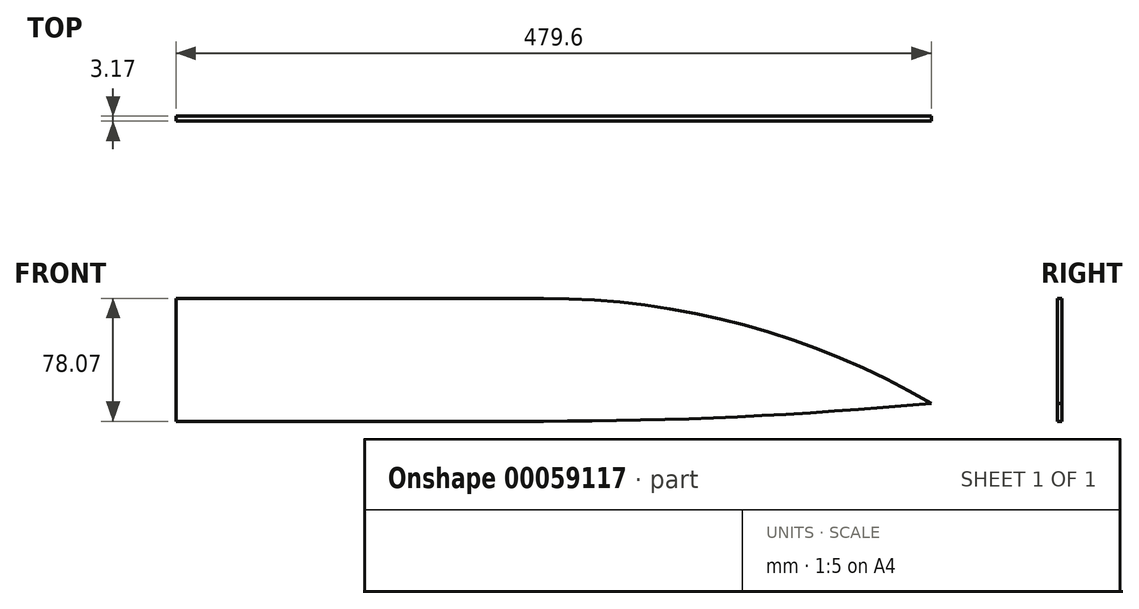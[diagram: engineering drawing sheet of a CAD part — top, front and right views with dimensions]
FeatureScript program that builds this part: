
annotation { "Feature Type Name" : "Feature", "Feature Type Description" : "" }
export const myFeature = defineFeature(function(context is Context, id is Id, definition is map)
    precondition{}
    {
        {
            var Q0;
            Q0=qCreatedBy(makeId("Front.planeOp"),FACE);
            var sketch = newSketch(context, id + "F0", { "sketchPlane" : qUnion([Q0])});
            skLineSegment(sketch, "E0", {"start": v(-232.64, 31.37) * mm, "end": v(0.7, 31.37) * mm});
            skLineSegment(sketch, "E1", {"start": v(-232.64, -46.7) * mm, "end": v(-232.64, 31.37) * mm});
            skLineSegment(sketch, "E2", {"start": v(0.7, -46.7) * mm, "end": v(-232.64, -46.7) * mm});
            skArc(sketch, "E3", {"start": v(246.96, -35.25) * mm, "mid": v(128.26, 14.42) * mm, "end": v(0.7, 31.37) * mm});
            skArc(sketch, "E4", {"start": v(0.7, -46.7) * mm, "mid": v(123.96, -43.83) * mm, "end": v(246.96, -35.25) * mm});
            skLineSegment(sketch, "E5", {"start": v(-232.12, 39.13) * mm, "end": v(250.48, 39.13) * mm, "construction": true});
            skSolve(sketch);
        }
        {
            var Q0;
            Q0 = qSketchRegion(id + "F0", true);
            extrude(context, id + "F1", {"entities" : qUnion([Q0]), "depth" : 3.17 * mm});
        }
    });
